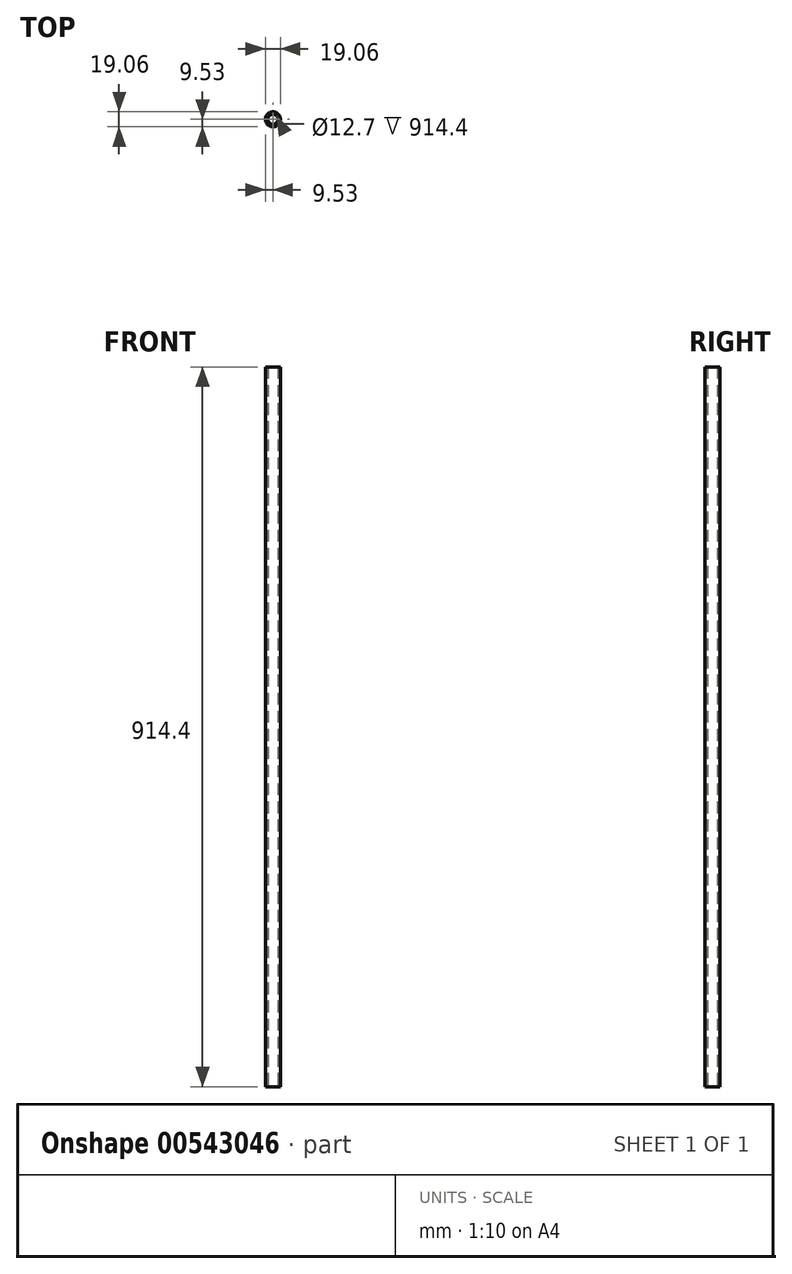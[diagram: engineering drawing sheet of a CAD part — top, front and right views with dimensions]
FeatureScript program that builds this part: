
annotation { "Feature Type Name" : "Feature", "Feature Type Description" : "" }
export const myFeature = defineFeature(function(context is Context, id is Id, definition is map)
    precondition{}
    {
        {
            var Q0;
            Q0=qCreatedBy(makeId("Top.planeOp"),FACE);
            var sketch = newSketch(context, id + "F0", { "sketchPlane" : qUnion([Q0])});
            skCircle(sketch, "E0", {"center": v(0, 0) * mm, "radius": 9.53 * mm});
            skCircle(sketch, "E1", {"center": v(0, 0) * mm, "radius": 6.35 * mm});
            skSolve(sketch);
        }
        {
            var Q0;
            Q0 = qSketchRegion(id + "F0", true);
            extrude(context, id + "F1", {"entities" : qUnion([Q0]), "depth" : 914.4 * mm, "offsetDistance" : 25.4 * mm});
        }
    });
